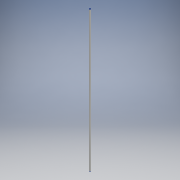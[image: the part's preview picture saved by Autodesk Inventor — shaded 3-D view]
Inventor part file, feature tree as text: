
AUTODESK INVENTOR PART (.ipt)
format: ipt  version: 2018 (Build 220112000, 112)  size: 92,160 bytes
history: native  units: mm
features: other x1, extrude x1, sketch x1
ambient origin geometry x8: Origin, YZ Plane, XZ Plane, XY Plane, X Axis, Y Axis, Z Axis, Center Point
bodies: Body1 (feature_tree)
feature tree (3):
  other  "ソリッド1"
  extrude  "押し出し1"  Depth=2.0mm
  sketch  "スケッチ1"
